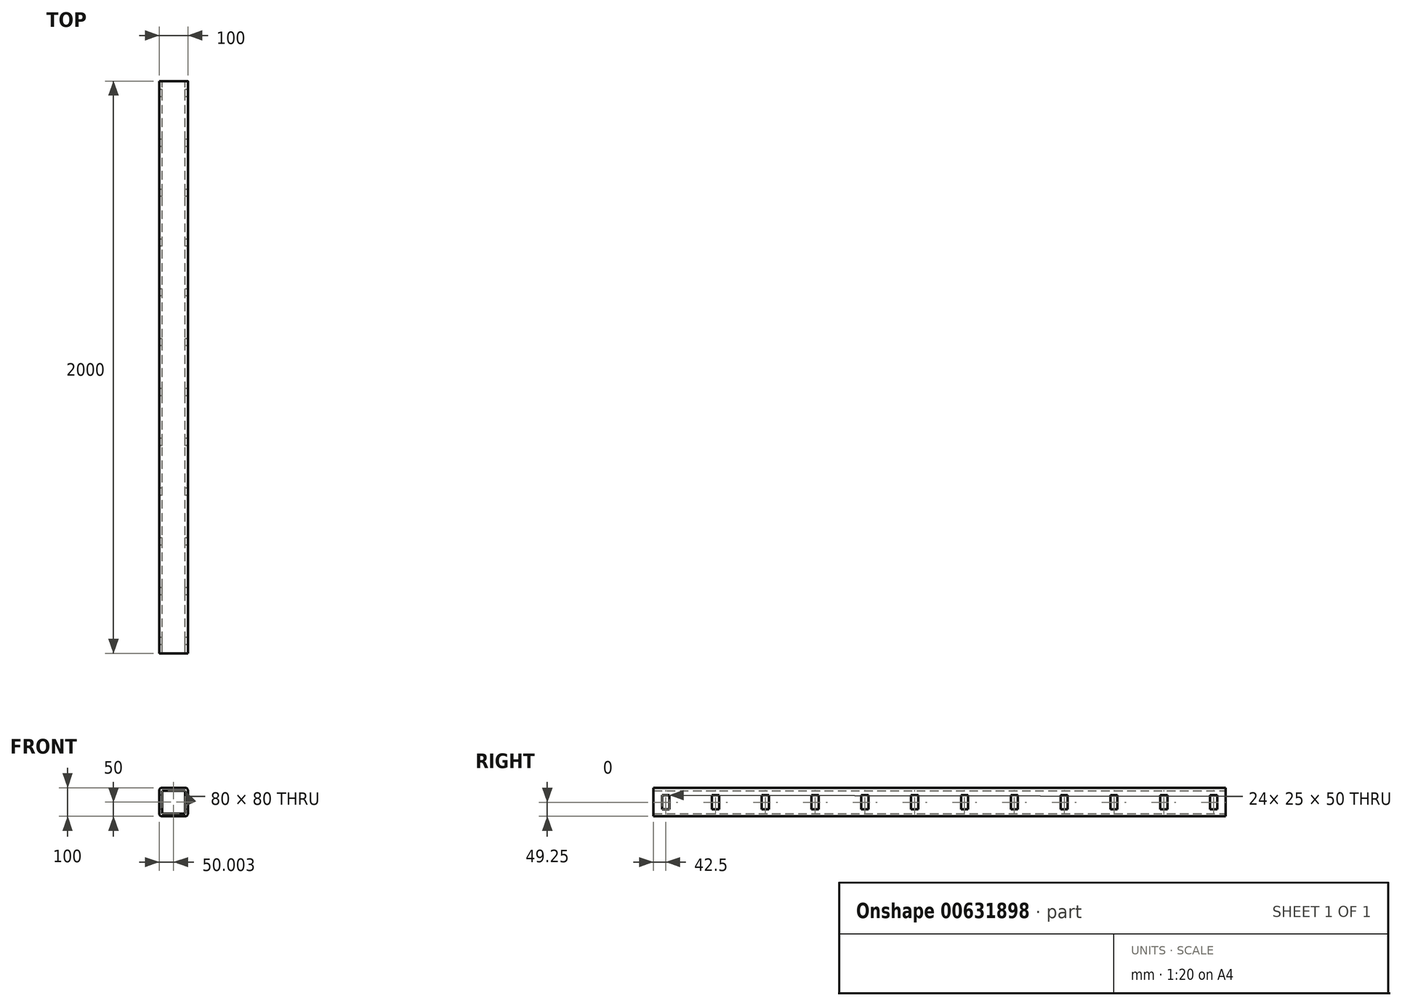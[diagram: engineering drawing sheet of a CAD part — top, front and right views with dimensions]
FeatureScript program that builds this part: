
annotation { "Feature Type Name" : "Feature", "Feature Type Description" : "" }
export const myFeature = defineFeature(function(context is Context, id is Id, definition is map)
    precondition{}
    {
        {
            var Q0;
            Q0=qCreatedBy(makeId("Front.planeOp"),FACE);
            var sketch = newSketch(context, id + "F0", { "sketchPlane" : qUnion([Q0])});
            skLineSegment(sketch, "E0.bottom", {"start": v(-59.76, 75.75) * mm, "end": v(20.24, 75.75) * mm});
            skLineSegment(sketch, "E0.top", {"start": v(-59.76, -24.25) * mm, "end": v(20.24, -24.25) * mm});
            skLineSegment(sketch, "E0.left", {"start": v(-69.76, 65.75) * mm, "end": v(-69.76, -14.25) * mm});
            skLineSegment(sketch, "E0.right", {"start": v(30.24, 65.75) * mm, "end": v(30.24, -14.25) * mm});
            skPoint(sketch, "E1.visualSharp", {"position": v(-69.76, 75.75) * mm});
            skArc(sketch, "E1.filletArc", {"start": v(-59.76, 75.75) * mm, "mid": v(-66.83, 72.82) * mm, "end": v(-69.76, 65.75) * mm});
            skPoint(sketch, "E2.visualSharp", {"position": v(30.24, 75.75) * mm});
            skArc(sketch, "E2.filletArc", {"start": v(30.24, 65.75) * mm, "mid": v(27.31, 72.82) * mm, "end": v(20.24, 75.75) * mm});
            skPoint(sketch, "E3.visualSharp", {"position": v(30.24, -24.25) * mm});
            skArc(sketch, "E3.filletArc", {"start": v(20.24, -24.25) * mm, "mid": v(27.31, -21.32) * mm, "end": v(30.24, -14.25) * mm});
            skPoint(sketch, "E4.visualSharp", {"position": v(-69.76, -24.25) * mm});
            skArc(sketch, "E4.filletArc", {"start": v(-69.76, -14.25) * mm, "mid": v(-66.83, -21.32) * mm, "end": v(-59.76, -24.25) * mm});
            skLineSegment(sketch, "E5.0", {"start": v(20.24, 65.75) * mm, "end": v(20.24, -14.25) * mm});
            skLineSegment(sketch, "E5.1", {"start": v(20.24, -14.25) * mm, "end": v(20.24, -14.25) * mm});
            skLineSegment(sketch, "E5.2", {"start": v(20.24, 65.75) * mm, "end": v(20.24, 65.75) * mm});
            skLineSegment(sketch, "E5.3", {"start": v(-59.76, -14.25) * mm, "end": v(20.24, -14.25) * mm});
            skLineSegment(sketch, "E5.4", {"start": v(-59.76, 65.75) * mm, "end": v(20.24, 65.75) * mm});
            skLineSegment(sketch, "E5.5", {"start": v(-59.76, 65.75) * mm, "end": v(-59.76, 65.75) * mm});
            skLineSegment(sketch, "E5.6", {"start": v(-59.76, 65.75) * mm, "end": v(-59.76, -14.25) * mm});
            skLineSegment(sketch, "E5.7", {"start": v(-59.76, -14.25) * mm, "end": v(-59.76, -14.25) * mm});
            skSolve(sketch);
        }
        {
            var Q0;
            Q0 = qSketchRegion(id + "F0", true);
            extrude(context, id + "F1", {"entities" : qUnion([Q0]), "depth" : 2000 * mm, "offsetDistance" : 25 * mm});
        }
        {
            var Q0;
            Q0=makeQuery(id+"F1.opExtrude","SWEPT_FACE",FACE,{"disambiguationData":[OSD([sQuery(id+"F0.wireOp",EDGE,"E0.left")])]});
            var sketch = newSketch(context, id + "F2", { "sketchPlane" : qUnion([Q0])});
            skLineSegment(sketch, "E6.bottom", {"start": v(30, 50) * mm, "end": v(55, 50) * mm});
            skLineSegment(sketch, "E6.top", {"start": v(30, 0) * mm, "end": v(55, 0) * mm});
            skLineSegment(sketch, "E6.left", {"start": v(30, 50) * mm, "end": v(30, 0) * mm});
            skLineSegment(sketch, "E6.right", {"start": v(55, 50) * mm, "end": v(55, 0) * mm});
            skLineSegment(sketch, "E7.bottom", {"start": v(204.1, 50) * mm, "end": v(229.1, 50) * mm});
            skLineSegment(sketch, "E7.top", {"start": v(204.1, 0) * mm, "end": v(229.1, 0) * mm});
            skLineSegment(sketch, "E7.left", {"start": v(204.1, 50) * mm, "end": v(204.1, 0) * mm});
            skLineSegment(sketch, "E7.right", {"start": v(229.1, 50) * mm, "end": v(229.1, 0) * mm});
            skLineSegment(sketch, "E8.bottom", {"start": v(378.18, 50) * mm, "end": v(403.18, 50) * mm});
            skLineSegment(sketch, "E8.top", {"start": v(378.18, 0) * mm, "end": v(403.18, 0) * mm});
            skLineSegment(sketch, "E8.left", {"start": v(378.18, 50) * mm, "end": v(378.18, 0) * mm});
            skLineSegment(sketch, "E8.right", {"start": v(403.18, 50) * mm, "end": v(403.18, 0) * mm});
            skLineSegment(sketch, "E9.bottom", {"start": v(552.27, 50) * mm, "end": v(577.27, 50) * mm});
            skLineSegment(sketch, "E9.top", {"start": v(552.27, 0) * mm, "end": v(577.27, 0) * mm});
            skLineSegment(sketch, "E9.left", {"start": v(552.27, 50) * mm, "end": v(552.27, 0) * mm});
            skLineSegment(sketch, "E9.right", {"start": v(577.27, 50) * mm, "end": v(577.27, 0) * mm});
            skLineSegment(sketch, "E10.bottom", {"start": v(1945, 50) * mm, "end": v(1970, 50) * mm});
            skLineSegment(sketch, "E10.top", {"start": v(1945, 0) * mm, "end": v(1970, 0) * mm});
            skLineSegment(sketch, "E10.left", {"start": v(1945, 50) * mm, "end": v(1945, 0) * mm});
            skLineSegment(sketch, "E10.right", {"start": v(1970, 50) * mm, "end": v(1970, 0) * mm});
            skLineSegment(sketch, "E11.bottom", {"start": v(726.36, 50) * mm, "end": v(751.36, 50) * mm});
            skLineSegment(sketch, "E11.top", {"start": v(726.36, 0) * mm, "end": v(751.36, 0) * mm});
            skLineSegment(sketch, "E11.left", {"start": v(726.36, 50) * mm, "end": v(726.36, 0) * mm});
            skLineSegment(sketch, "E11.right", {"start": v(751.36, 50) * mm, "end": v(751.36, 0) * mm});
            skLineSegment(sketch, "E12.bottom", {"start": v(900.46, 50) * mm, "end": v(925.46, 50) * mm});
            skLineSegment(sketch, "E12.top", {"start": v(900.46, 0) * mm, "end": v(925.46, 0) * mm});
            skLineSegment(sketch, "E12.left", {"start": v(900.46, 50) * mm, "end": v(900.46, 0) * mm});
            skLineSegment(sketch, "E12.right", {"start": v(925.46, 50) * mm, "end": v(925.46, 0) * mm});
            skLineSegment(sketch, "E13.bottom", {"start": v(1074.55, 50) * mm, "end": v(1099.55, 50) * mm});
            skLineSegment(sketch, "E13.top", {"start": v(1074.55, 0) * mm, "end": v(1099.55, 0) * mm});
            skLineSegment(sketch, "E13.left", {"start": v(1074.55, 50) * mm, "end": v(1074.55, 0) * mm});
            skLineSegment(sketch, "E13.right", {"start": v(1099.55, 50) * mm, "end": v(1099.55, 0) * mm});
            skLineSegment(sketch, "E14.bottom", {"start": v(1248.64, 50) * mm, "end": v(1273.64, 50) * mm});
            skLineSegment(sketch, "E14.top", {"start": v(1248.64, 0) * mm, "end": v(1273.64, 0) * mm});
            skLineSegment(sketch, "E14.left", {"start": v(1248.64, 50) * mm, "end": v(1248.64, 0) * mm});
            skLineSegment(sketch, "E14.right", {"start": v(1273.64, 50) * mm, "end": v(1273.64, 0) * mm});
            skLineSegment(sketch, "E15.bottom", {"start": v(1422.73, 50) * mm, "end": v(1447.73, 50) * mm});
            skLineSegment(sketch, "E15.top", {"start": v(1422.73, 0) * mm, "end": v(1447.73, 0) * mm});
            skLineSegment(sketch, "E15.left", {"start": v(1422.73, 50) * mm, "end": v(1422.73, 0) * mm});
            skLineSegment(sketch, "E15.right", {"start": v(1447.73, 50) * mm, "end": v(1447.73, 0) * mm});
            skLineSegment(sketch, "E16.bottom", {"start": v(1596.82, 50) * mm, "end": v(1621.82, 50) * mm});
            skLineSegment(sketch, "E16.top", {"start": v(1596.82, 0) * mm, "end": v(1621.82, 0) * mm});
            skLineSegment(sketch, "E16.left", {"start": v(1596.82, 50) * mm, "end": v(1596.82, 0) * mm});
            skLineSegment(sketch, "E16.right", {"start": v(1621.82, 50) * mm, "end": v(1621.82, 0) * mm});
            skLineSegment(sketch, "E17.bottom", {"start": v(1770.9, 50) * mm, "end": v(1795.9, 50) * mm});
            skLineSegment(sketch, "E17.top", {"start": v(1770.9, 0) * mm, "end": v(1795.9, 0) * mm});
            skLineSegment(sketch, "E17.left", {"start": v(1770.9, 50) * mm, "end": v(1770.9, 0) * mm});
            skLineSegment(sketch, "E17.right", {"start": v(1795.9, 50) * mm, "end": v(1795.9, 0) * mm});
            skSolve(sketch);
        }
        {
            var Q0;
            Q0 = qSketchRegion(id + "F2", true);
            extrude(context, id + "F3", {"entities" : qUnion([Q0]), "operationType" : NewBodyOperationType.REMOVE, "oppositeDirection" : true, "depth" : 100 * mm, "offsetDistance" : 25 * mm});
        }
    });
